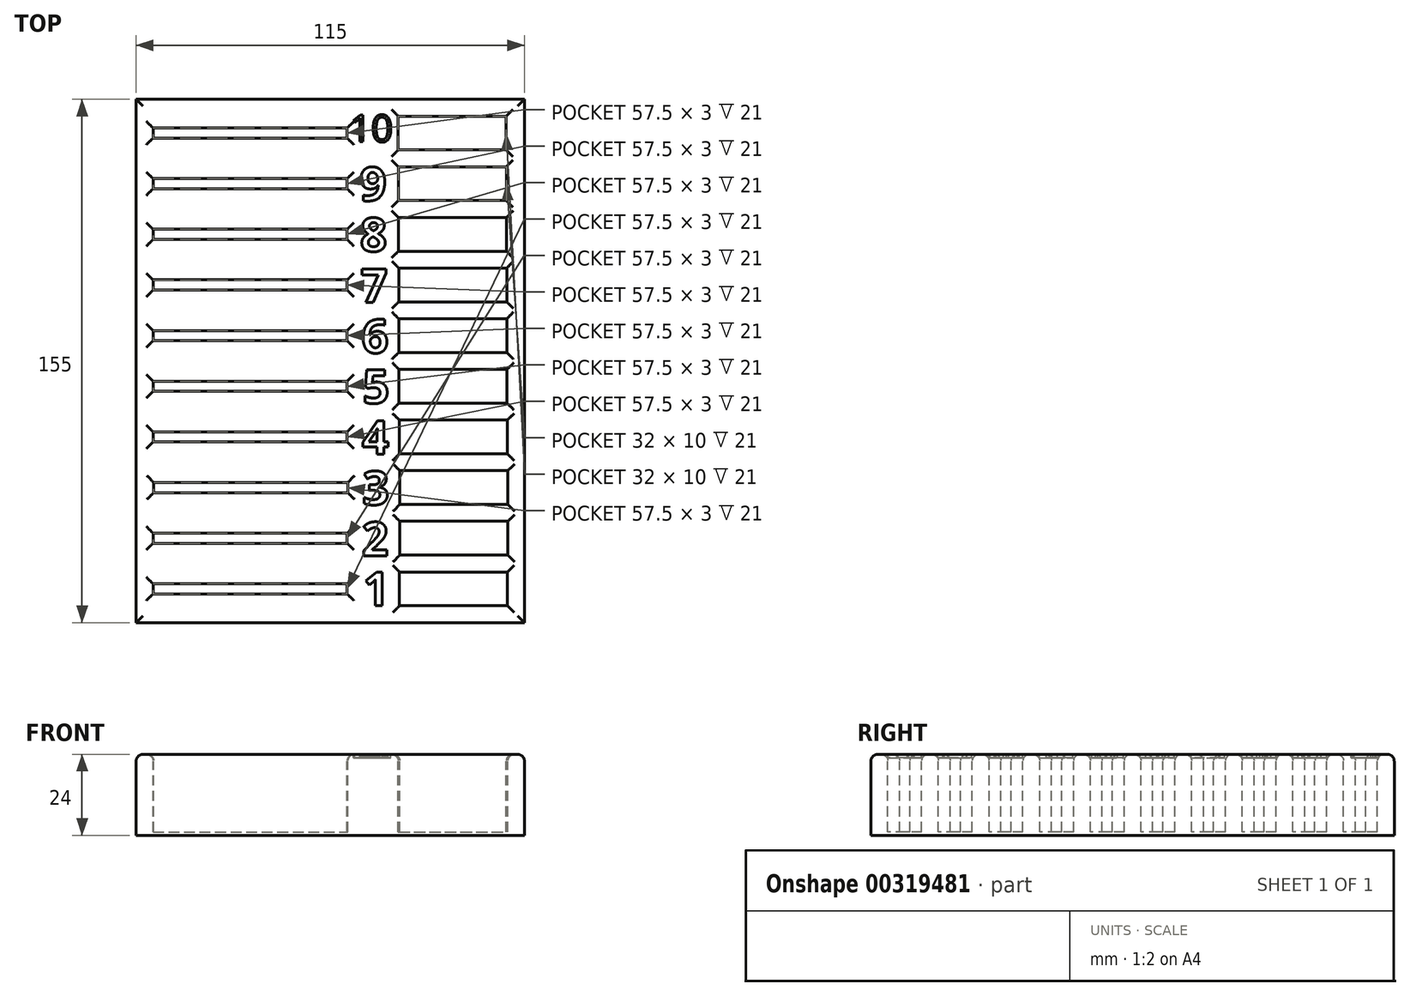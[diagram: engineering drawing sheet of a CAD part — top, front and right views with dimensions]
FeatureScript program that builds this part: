
annotation { "Feature Type Name" : "Feature", "Feature Type Description" : "" }
export const myFeature = defineFeature(function(context is Context, id is Id, definition is map)
    precondition{}
    {
        {
            var Q0;
            Q0=qCreatedBy(makeId("Top.planeOp"),FACE);
            var sketch = newSketch(context, id + "F0", { "sketchPlane" : qUnion([Q0])});
            skLineSegment(sketch, "E0.bottom", {"start": v(-49.85, 126.63) * mm, "end": v(65.15, 126.63) * mm});
            skLineSegment(sketch, "E0.top", {"start": v(-49.85, -28.37) * mm, "end": v(65.15, -28.37) * mm});
            skLineSegment(sketch, "E0.left", {"start": v(-49.85, 126.63) * mm, "end": v(-49.85, -28.37) * mm});
            skLineSegment(sketch, "E0.right", {"start": v(65.15, 126.63) * mm, "end": v(65.15, -28.37) * mm});
            skSolve(sketch);
        }
        {
            var Q0;
            Q0=makeQuery(id+"F0.imprint","IMPRINT",FACE,{"disambiguationData":[TD([[makeQuery(id+"F0.imprint","IMPRINT",EDGE,{"derivedFrom":sQuery(id+"F0.wireOp",EDGE,"E0.bottom")}),-1.0]])]});
            var Q1;
            Q1=makeQuery(id+"F0.imprint","IMPRINT",FACE,{"disambiguationData":[TD([[makeQuery(id+"F0.imprint","IMPRINT",EDGE,{"derivedFrom":sQuery(id+"F0.wireOp",EDGE,"eXpO4zti-W6eb-gkUP-Bc0d-zbJJjk6ygzeg.bottom")}),-1.0]])]});
            var Q2;
            Q2=makeQuery(id+"F0.imprint","IMPRINT",FACE,{"disambiguationData":[TD([[makeQuery(id+"F0.imprint","IMPRINT",EDGE,{"derivedFrom":sQuery(id+"F0.wireOp",EDGE,"IiJkesfC-iyIp-GpGT-9vFS-BzQ84R5pHUzr.bottom")}),-1.0]])]});
            extrude(context, id + "F1", {"entities" : qUnion([Q0, Q1, Q2]), "depth" : 24 * mm});
        }
        {
            var Q0;
            Q0=makeQuery(id+"F1.opExtrude","CAP_FACE",FACE,{"disambiguationData":[OSD([sQuery(id+"F0.wireOp",EDGE,"E0.bottom"),sQuery(id+"F0.wireOp",EDGE,"E0.top"),sQuery(id+"F0.wireOp",EDGE,"E0.left"),sQuery(id+"F0.wireOp",EDGE,"E0.right")])],"isStart":false});
            var sketch = newSketch(context, id + "F2", { "sketchPlane" : qUnion([Q0])});
            skLineSegment(sketch, "E1.bottom", {"start": v(-44.85, -16.87) * mm, "end": v(12.65, -16.87) * mm});
            skLineSegment(sketch, "E1.top", {"start": v(-44.85, -19.87) * mm, "end": v(12.65, -19.87) * mm});
            skLineSegment(sketch, "E1.left", {"start": v(-44.85, -16.87) * mm, "end": v(-44.85, -19.87) * mm});
            skLineSegment(sketch, "E1.right", {"start": v(12.65, -16.87) * mm, "end": v(12.65, -19.87) * mm});
            skLineSegment(sketch, "E2.bottom", {"start": v(28.15, -13.37) * mm, "end": v(60.15, -13.37) * mm});
            skLineSegment(sketch, "E2.top", {"start": v(28.15, -23.37) * mm, "end": v(60.15, -23.37) * mm});
            skLineSegment(sketch, "E2.left", {"start": v(28.15, -13.37) * mm, "end": v(28.15, -23.37) * mm});
            skLineSegment(sketch, "E2.right", {"start": v(60.15, -13.37) * mm, "end": v(60.15, -23.37) * mm});
            skText(sketch, "E3", { "text": "1", "fontName": "OpenSans-Bold.ttf"});
            skLineSegment(sketch, "E4.bottom", {"start": v(-44.87, -1.87) * mm, "end": v(12.63, -1.87) * mm});
            skLineSegment(sketch, "E4.top", {"start": v(-44.87, -4.87) * mm, "end": v(12.63, -4.87) * mm});
            skLineSegment(sketch, "E4.left", {"start": v(-44.87, -1.87) * mm, "end": v(-44.87, -4.87) * mm});
            skLineSegment(sketch, "E4.right", {"start": v(12.63, -1.87) * mm, "end": v(12.63, -4.87) * mm});
            skLineSegment(sketch, "E5.bottom", {"start": v(28.23, 1.63) * mm, "end": v(60.23, 1.63) * mm});
            skLineSegment(sketch, "E5.top", {"start": v(28.23, -8.37) * mm, "end": v(60.23, -8.37) * mm});
            skLineSegment(sketch, "E5.left", {"start": v(28.23, 1.63) * mm, "end": v(28.23, -8.37) * mm});
            skLineSegment(sketch, "E5.right", {"start": v(60.23, 1.63) * mm, "end": v(60.23, -8.37) * mm});
            skLineSegment(sketch, "E6.bottom", {"start": v(28.24, 16.63) * mm, "end": v(60.24, 16.63) * mm});
            skLineSegment(sketch, "E6.top", {"start": v(28.24, 6.63) * mm, "end": v(60.24, 6.63) * mm});
            skLineSegment(sketch, "E6.left", {"start": v(28.24, 16.63) * mm, "end": v(28.24, 6.63) * mm});
            skLineSegment(sketch, "E6.right", {"start": v(60.24, 16.63) * mm, "end": v(60.24, 6.63) * mm});
            skLineSegment(sketch, "E7.bottom", {"start": v(28.1, 31.63) * mm, "end": v(60.1, 31.63) * mm});
            skLineSegment(sketch, "E7.top", {"start": v(28.1, 21.63) * mm, "end": v(60.1, 21.63) * mm});
            skLineSegment(sketch, "E7.left", {"start": v(28.1, 31.63) * mm, "end": v(28.1, 21.63) * mm});
            skLineSegment(sketch, "E7.right", {"start": v(60.1, 31.63) * mm, "end": v(60.1, 21.63) * mm});
            skLineSegment(sketch, "E8.bottom", {"start": v(28, 46.63) * mm, "end": v(60, 46.63) * mm});
            skLineSegment(sketch, "E8.top", {"start": v(28, 36.63) * mm, "end": v(60, 36.63) * mm});
            skLineSegment(sketch, "E8.left", {"start": v(28, 46.63) * mm, "end": v(28, 36.63) * mm});
            skLineSegment(sketch, "E8.right", {"start": v(60, 46.63) * mm, "end": v(60, 36.63) * mm});
            skLineSegment(sketch, "E9.bottom", {"start": v(27.93, 61.63) * mm, "end": v(59.93, 61.63) * mm});
            skLineSegment(sketch, "E9.top", {"start": v(27.93, 51.63) * mm, "end": v(59.93, 51.63) * mm});
            skLineSegment(sketch, "E9.left", {"start": v(27.93, 61.63) * mm, "end": v(27.93, 51.63) * mm});
            skLineSegment(sketch, "E9.right", {"start": v(59.93, 61.63) * mm, "end": v(59.93, 51.63) * mm});
            skLineSegment(sketch, "E10.bottom", {"start": v(27.91, 76.63) * mm, "end": v(59.91, 76.63) * mm});
            skLineSegment(sketch, "E10.top", {"start": v(27.91, 66.63) * mm, "end": v(59.91, 66.63) * mm});
            skLineSegment(sketch, "E10.left", {"start": v(27.91, 76.63) * mm, "end": v(27.91, 66.63) * mm});
            skLineSegment(sketch, "E10.right", {"start": v(59.91, 76.63) * mm, "end": v(59.91, 66.63) * mm});
            skLineSegment(sketch, "E11.bottom", {"start": v(27.82, 91.63) * mm, "end": v(59.82, 91.63) * mm});
            skLineSegment(sketch, "E11.top", {"start": v(27.82, 81.63) * mm, "end": v(59.82, 81.63) * mm});
            skLineSegment(sketch, "E11.left", {"start": v(27.82, 91.63) * mm, "end": v(27.82, 81.63) * mm});
            skLineSegment(sketch, "E11.right", {"start": v(59.82, 91.63) * mm, "end": v(59.82, 81.63) * mm});
            skLineSegment(sketch, "E12.bottom", {"start": v(27.78, 106.63) * mm, "end": v(59.78, 106.63) * mm});
            skLineSegment(sketch, "E12.top", {"start": v(27.78, 96.63) * mm, "end": v(59.78, 96.63) * mm});
            skLineSegment(sketch, "E12.left", {"start": v(27.78, 106.63) * mm, "end": v(27.78, 96.63) * mm});
            skLineSegment(sketch, "E12.right", {"start": v(59.78, 106.63) * mm, "end": v(59.78, 96.63) * mm});
            skLineSegment(sketch, "E13.bottom", {"start": v(27.76, 121.63) * mm, "end": v(59.76, 121.63) * mm});
            skLineSegment(sketch, "E13.top", {"start": v(27.76, 111.63) * mm, "end": v(59.76, 111.63) * mm});
            skLineSegment(sketch, "E13.left", {"start": v(27.76, 121.63) * mm, "end": v(27.76, 111.63) * mm});
            skLineSegment(sketch, "E13.right", {"start": v(59.76, 121.63) * mm, "end": v(59.76, 111.63) * mm});
            skLineSegment(sketch, "E14.bottom", {"start": v(-44.66, 13.13) * mm, "end": v(12.84, 13.13) * mm});
            skLineSegment(sketch, "E14.top", {"start": v(-44.66, 10.13) * mm, "end": v(12.84, 10.13) * mm});
            skLineSegment(sketch, "E14.left", {"start": v(-44.66, 13.13) * mm, "end": v(-44.66, 10.13) * mm});
            skLineSegment(sketch, "E14.right", {"start": v(12.84, 13.13) * mm, "end": v(12.84, 10.13) * mm});
            skLineSegment(sketch, "E15.bottom", {"start": v(-44.85, 28.13) * mm, "end": v(12.65, 28.13) * mm});
            skLineSegment(sketch, "E15.top", {"start": v(-44.85, 25.13) * mm, "end": v(12.65, 25.13) * mm});
            skLineSegment(sketch, "E15.left", {"start": v(-44.85, 28.13) * mm, "end": v(-44.85, 25.13) * mm});
            skLineSegment(sketch, "E15.right", {"start": v(12.65, 28.13) * mm, "end": v(12.65, 25.13) * mm});
            skLineSegment(sketch, "E16.bottom", {"start": v(-44.85, 43.13) * mm, "end": v(12.65, 43.13) * mm});
            skLineSegment(sketch, "E16.top", {"start": v(-44.85, 40.13) * mm, "end": v(12.65, 40.13) * mm});
            skLineSegment(sketch, "E16.left", {"start": v(-44.85, 43.13) * mm, "end": v(-44.85, 40.13) * mm});
            skLineSegment(sketch, "E16.right", {"start": v(12.65, 43.13) * mm, "end": v(12.65, 40.13) * mm});
            skLineSegment(sketch, "E17.bottom", {"start": v(-44.85, 58.13) * mm, "end": v(12.65, 58.13) * mm});
            skLineSegment(sketch, "E17.top", {"start": v(-44.85, 55.13) * mm, "end": v(12.65, 55.13) * mm});
            skLineSegment(sketch, "E17.left", {"start": v(-44.85, 58.13) * mm, "end": v(-44.85, 55.13) * mm});
            skLineSegment(sketch, "E17.right", {"start": v(12.65, 58.13) * mm, "end": v(12.65, 55.13) * mm});
            skLineSegment(sketch, "E18.bottom", {"start": v(-44.85, 73.13) * mm, "end": v(12.65, 73.13) * mm});
            skLineSegment(sketch, "E18.top", {"start": v(-44.85, 70.13) * mm, "end": v(12.65, 70.13) * mm});
            skLineSegment(sketch, "E18.left", {"start": v(-44.85, 73.13) * mm, "end": v(-44.85, 70.13) * mm});
            skLineSegment(sketch, "E18.right", {"start": v(12.65, 73.13) * mm, "end": v(12.65, 70.13) * mm});
            skLineSegment(sketch, "E19.bottom", {"start": v(-44.85, 88.13) * mm, "end": v(12.65, 88.13) * mm});
            skLineSegment(sketch, "E19.top", {"start": v(-44.85, 85.13) * mm, "end": v(12.65, 85.13) * mm});
            skLineSegment(sketch, "E19.left", {"start": v(-44.85, 88.13) * mm, "end": v(-44.85, 85.13) * mm});
            skLineSegment(sketch, "E19.right", {"start": v(12.65, 88.13) * mm, "end": v(12.65, 85.13) * mm});
            skLineSegment(sketch, "E20.bottom", {"start": v(-44.85, 103.13) * mm, "end": v(12.65, 103.13) * mm});
            skLineSegment(sketch, "E20.top", {"start": v(-44.85, 100.13) * mm, "end": v(12.65, 100.13) * mm});
            skLineSegment(sketch, "E20.left", {"start": v(-44.85, 103.13) * mm, "end": v(-44.85, 100.13) * mm});
            skLineSegment(sketch, "E20.right", {"start": v(12.65, 103.13) * mm, "end": v(12.65, 100.13) * mm});
            skLineSegment(sketch, "E21.bottom", {"start": v(-44.85, 118.13) * mm, "end": v(12.65, 118.13) * mm});
            skLineSegment(sketch, "E21.top", {"start": v(-44.85, 115.13) * mm, "end": v(12.65, 115.13) * mm});
            skLineSegment(sketch, "E21.left", {"start": v(-44.85, 118.13) * mm, "end": v(-44.85, 115.13) * mm});
            skLineSegment(sketch, "E21.right", {"start": v(12.65, 118.13) * mm, "end": v(12.65, 115.13) * mm});
            skText(sketch, "E22", { "text": "2", "fontName": "OpenSans-Bold.ttf"});
            skText(sketch, "E23", { "text": "3", "fontName": "OpenSans-Bold.ttf"});
            skText(sketch, "E24", { "text": "4", "fontName": "OpenSans-Bold.ttf"});
            skText(sketch, "E25", { "text": "5", "fontName": "OpenSans-Bold.ttf"});
            skText(sketch, "E26", { "text": "6", "fontName": "OpenSans-Bold.ttf"});
            skText(sketch, "E27", { "text": "7", "fontName": "OpenSans-Bold.ttf"});
            skText(sketch, "E28", { "text": "8", "fontName": "OpenSans-Bold.ttf"});
            skText(sketch, "E29", { "text": "9", "fontName": "OpenSans-Bold.ttf"});
            skText(sketch, "E30", { "text": "10", "fontName": "OpenSans-Regular.ttf"});
            const initialGuessF2  = {"E3": [0.01732, -0.02332, 1, 0, 0.01], "E22": [0.01698, -0.00854, 1, 0, 0.01], "E23": [0.01713, 0.00655, 1, 0, 0.01], "E24": [0.01702, 0.02156, 1, 0, 0.01], "E25": [0.0172, 0.03658, 1, 0, 0.01], "E26": [0.01692, 0.0515, 1, 0, 0.01], "E27": [0.01664, 0.06649, 1, 0, 0.01], "E28": [0.01648, 0.08158, 1, 0, 0.01], "E29": [0.01632, 0.0966, 1, 0, 0.01], "E30": [0.01344, 0.11403, 1, 0, 0.008]};
            skSetInitialGuess(sketch, initialGuessF2);
            skSolve(sketch);
        }
        {
            var Q0;
            Q0=makeQuery(id+"F2.imprint","IMPRINT",FACE,{"disambiguationData":[TD([[makeQuery(id+"F2.imprint","IMPRINT",EDGE,{"derivedFrom":sQuery(id+"F2.wireOp",EDGE,"E2.bottom")}),-1.0]])]});
            var Q1;
            Q1=makeQuery(id+"F2.imprint","IMPRINT",FACE,{"disambiguationData":[TD([[makeQuery(id+"F2.imprint","IMPRINT",EDGE,{"derivedFrom":sQuery(id+"F2.wireOp",EDGE,"E1.bottom")}),-1.0]])]});
            var Q2;
            Q2=makeQuery(id+"F2.imprint","IMPRINT",FACE,{"disambiguationData":[TD([[makeQuery(id+"F2.imprint","IMPRINT",EDGE,{"derivedFrom":sQuery(id+"F2.wireOp",EDGE,"E4.bottom")}),-1.0]])]});
            var Q3;
            Q3=makeQuery(id+"F2.imprint","IMPRINT",FACE,{"disambiguationData":[TD([[makeQuery(id+"F2.imprint","IMPRINT",EDGE,{"derivedFrom":sQuery(id+"F2.wireOp",EDGE,"E5.bottom")}),-1.0]])]});
            var Q4;
            Q4=makeQuery(id+"F2.imprint","IMPRINT",FACE,{"disambiguationData":[TD([[makeQuery(id+"F2.imprint","IMPRINT",EDGE,{"derivedFrom":sQuery(id+"F2.wireOp",EDGE,"E6.bottom")}),-1.0]])]});
            var Q5;
            Q5=makeQuery(id+"F2.imprint","IMPRINT",FACE,{"disambiguationData":[TD([[makeQuery(id+"F2.imprint","IMPRINT",EDGE,{"derivedFrom":sQuery(id+"F2.wireOp",EDGE,"E7.bottom")}),-1.0]])]});
            var Q6;
            Q6=makeQuery(id+"F2.imprint","IMPRINT",FACE,{"disambiguationData":[TD([[makeQuery(id+"F2.imprint","IMPRINT",EDGE,{"derivedFrom":sQuery(id+"F2.wireOp",EDGE,"E8.bottom")}),-1.0]])]});
            var Q7;
            Q7=makeQuery(id+"F2.imprint","IMPRINT",FACE,{"disambiguationData":[TD([[makeQuery(id+"F2.imprint","IMPRINT",EDGE,{"derivedFrom":sQuery(id+"F2.wireOp",EDGE,"E9.bottom")}),-1.0]])]});
            var Q8;
            Q8=makeQuery(id+"F2.imprint","IMPRINT",FACE,{"disambiguationData":[TD([[makeQuery(id+"F2.imprint","IMPRINT",EDGE,{"derivedFrom":sQuery(id+"F2.wireOp",EDGE,"E10.bottom")}),-1.0]])]});
            var Q9;
            Q9=makeQuery(id+"F2.imprint","IMPRINT",FACE,{"disambiguationData":[TD([[makeQuery(id+"F2.imprint","IMPRINT",EDGE,{"derivedFrom":sQuery(id+"F2.wireOp",EDGE,"E11.bottom")}),-1.0]])]});
            var Q10;
            Q10=makeQuery(id+"F2.imprint","IMPRINT",FACE,{"disambiguationData":[TD([[makeQuery(id+"F2.imprint","IMPRINT",EDGE,{"derivedFrom":sQuery(id+"F2.wireOp",EDGE,"E12.bottom")}),-1.0]])]});
            var Q11;
            Q11=makeQuery(id+"F2.imprint","IMPRINT",FACE,{"disambiguationData":[TD([[makeQuery(id+"F2.imprint","IMPRINT",EDGE,{"derivedFrom":sQuery(id+"F2.wireOp",EDGE,"E13.bottom")}),-1.0]])]});
            var Q12;
            Q12=makeQuery(id+"F2.imprint","IMPRINT",FACE,{"disambiguationData":[TD([[makeQuery(id+"F2.imprint","IMPRINT",EDGE,{"derivedFrom":sQuery(id+"F2.wireOp",EDGE,"E14.bottom")}),-1.0]])]});
            var Q13;
            Q13=makeQuery(id+"F2.imprint","IMPRINT",FACE,{"disambiguationData":[TD([[makeQuery(id+"F2.imprint","IMPRINT",EDGE,{"derivedFrom":sQuery(id+"F2.wireOp",EDGE,"E15.bottom")}),-1.0]])]});
            var Q14;
            Q14=makeQuery(id+"F2.imprint","IMPRINT",FACE,{"disambiguationData":[TD([[makeQuery(id+"F2.imprint","IMPRINT",EDGE,{"derivedFrom":sQuery(id+"F2.wireOp",EDGE,"E16.bottom")}),-1.0]])]});
            var Q15;
            Q15=makeQuery(id+"F2.imprint","IMPRINT",FACE,{"disambiguationData":[TD([[makeQuery(id+"F2.imprint","IMPRINT",EDGE,{"derivedFrom":sQuery(id+"F2.wireOp",EDGE,"E17.bottom")}),-1.0]])]});
            var Q16;
            Q16=makeQuery(id+"F2.imprint","IMPRINT",FACE,{"disambiguationData":[TD([[makeQuery(id+"F2.imprint","IMPRINT",EDGE,{"derivedFrom":sQuery(id+"F2.wireOp",EDGE,"E18.bottom")}),-1.0]])]});
            var Q17;
            Q17=makeQuery(id+"F2.imprint","IMPRINT",FACE,{"disambiguationData":[TD([[makeQuery(id+"F2.imprint","IMPRINT",EDGE,{"derivedFrom":sQuery(id+"F2.wireOp",EDGE,"E19.bottom")}),-1.0]])]});
            var Q18;
            Q18=makeQuery(id+"F2.imprint","IMPRINT",FACE,{"disambiguationData":[TD([[makeQuery(id+"F2.imprint","IMPRINT",EDGE,{"derivedFrom":sQuery(id+"F2.wireOp",EDGE,"E20.bottom")}),-1.0]])]});
            var Q19;
            Q19=makeQuery(id+"F2.imprint","IMPRINT",FACE,{"disambiguationData":[TD([[makeQuery(id+"F2.imprint","IMPRINT",EDGE,{"derivedFrom":sQuery(id+"F2.wireOp",EDGE,"E21.bottom")}),-1.0]])]});
            extrude(context, id + "F3", {"entities" : qUnion([Q0, Q1, Q2, Q3, Q4, Q5, Q6, Q7, Q8, Q9, Q10, Q11, Q12, Q13, Q14, Q15, Q16, Q17, Q18, Q19]), "operationType" : NewBodyOperationType.REMOVE, "oppositeDirection" : true, "depth" : 23 * mm});
        }
        {
            var Q0;
            Q0=makeQuery(id+"F3.boolean.opBoolean","COPY",EDGE,{"derivedFrom":makeQuery(id+"F3.opExtrude","CAP_EDGE",EDGE,{"disambiguationData":[OSD([sQuery(id+"F2.wireOp",EDGE,"E1.top")])],"isStart":true})});
            var Q1;
            Q1=makeQuery(id+"F3.boolean.opBoolean","COPY",EDGE,{"derivedFrom":makeQuery(id+"F3.opExtrude","CAP_EDGE",EDGE,{"disambiguationData":[OSD([sQuery(id+"F2.wireOp",EDGE,"E1.bottom")])],"isStart":true})});
            var Q2;
            Q2=makeQuery(id+"F3.boolean.opBoolean","COPY",EDGE,{"derivedFrom":makeQuery(id+"F3.opExtrude","CAP_EDGE",EDGE,{"disambiguationData":[OSD([sQuery(id+"F2.wireOp",EDGE,"E1.right")])],"isStart":true})});
            var Q3;
            Q3=makeQuery(id+"F3.boolean.opBoolean","COPY",EDGE,{"derivedFrom":makeQuery(id+"F3.opExtrude","CAP_EDGE",EDGE,{"disambiguationData":[OSD([sQuery(id+"F2.wireOp",EDGE,"E1.left")])],"isStart":true})});
            var Q4;
            Q4=makeQuery(id+"F3.boolean.opBoolean","COPY",EDGE,{"derivedFrom":makeQuery(id+"F3.opExtrude","CAP_EDGE",EDGE,{"disambiguationData":[OSD([sQuery(id+"F2.wireOp",EDGE,"E2.bottom")])],"isStart":true})});
            var Q5;
            Q5=makeQuery(id+"F3.boolean.opBoolean","COPY",EDGE,{"derivedFrom":makeQuery(id+"F3.opExtrude","CAP_EDGE",EDGE,{"disambiguationData":[OSD([sQuery(id+"F2.wireOp",EDGE,"E2.top")])],"isStart":true})});
            var Q6;
            Q6=makeQuery(id+"F3.boolean.opBoolean","COPY",EDGE,{"derivedFrom":makeQuery(id+"F3.opExtrude","CAP_EDGE",EDGE,{"disambiguationData":[OSD([sQuery(id+"F2.wireOp",EDGE,"E2.left")])],"isStart":true})});
            var Q7;
            Q7=makeQuery(id+"F3.boolean.opBoolean","COPY",EDGE,{"derivedFrom":makeQuery(id+"F3.opExtrude","CAP_EDGE",EDGE,{"disambiguationData":[OSD([sQuery(id+"F2.wireOp",EDGE,"E2.right")])],"isStart":true})});
            var Q8;
            Q8=makeQuery(id+"F3.boolean.opBoolean","COPY",EDGE,{"derivedFrom":makeQuery(id+"F3.opExtrude","CAP_EDGE",EDGE,{"disambiguationData":[OSD([sQuery(id+"F2.wireOp",EDGE,"E4.bottom")])],"isStart":true})});
            var Q9;
            Q9=makeQuery(id+"F3.boolean.opBoolean","COPY",EDGE,{"derivedFrom":makeQuery(id+"F3.opExtrude","CAP_EDGE",EDGE,{"disambiguationData":[OSD([sQuery(id+"F2.wireOp",EDGE,"E4.top")])],"isStart":true})});
            var Q10;
            Q10=makeQuery(id+"F3.boolean.opBoolean","COPY",EDGE,{"derivedFrom":makeQuery(id+"F3.opExtrude","CAP_EDGE",EDGE,{"disambiguationData":[OSD([sQuery(id+"F2.wireOp",EDGE,"E4.left")])],"isStart":true})});
            var Q11;
            Q11=makeQuery(id+"F3.boolean.opBoolean","COPY",EDGE,{"derivedFrom":makeQuery(id+"F3.opExtrude","CAP_EDGE",EDGE,{"disambiguationData":[OSD([sQuery(id+"F2.wireOp",EDGE,"E4.right")])],"isStart":true})});
            var Q12;
            Q12=makeQuery(id+"F3.boolean.opBoolean","COPY",EDGE,{"derivedFrom":makeQuery(id+"F3.opExtrude","CAP_EDGE",EDGE,{"disambiguationData":[OSD([sQuery(id+"F2.wireOp",EDGE,"E5.left")])],"isStart":true})});
            var Q13;
            Q13=makeQuery(id+"F3.boolean.opBoolean","COPY",EDGE,{"derivedFrom":makeQuery(id+"F3.opExtrude","CAP_EDGE",EDGE,{"disambiguationData":[OSD([sQuery(id+"F2.wireOp",EDGE,"E5.bottom")])],"isStart":true})});
            var Q14;
            Q14=makeQuery(id+"F3.boolean.opBoolean","COPY",EDGE,{"derivedFrom":makeQuery(id+"F3.opExtrude","CAP_EDGE",EDGE,{"disambiguationData":[OSD([sQuery(id+"F2.wireOp",EDGE,"E5.right")])],"isStart":true})});
            var Q15;
            Q15=makeQuery(id+"F3.boolean.opBoolean","COPY",EDGE,{"derivedFrom":makeQuery(id+"F3.opExtrude","CAP_EDGE",EDGE,{"disambiguationData":[OSD([sQuery(id+"F2.wireOp",EDGE,"E5.top")])],"isStart":true})});
            var Q16;
            Q16=makeQuery(id+"F3.boolean.opBoolean","COPY",EDGE,{"derivedFrom":makeQuery(id+"F3.opExtrude","CAP_EDGE",EDGE,{"disambiguationData":[OSD([sQuery(id+"F2.wireOp",EDGE,"E6.top")])],"isStart":true})});
            var Q17;
            Q17=makeQuery(id+"F3.boolean.opBoolean","COPY",EDGE,{"derivedFrom":makeQuery(id+"F3.opExtrude","CAP_EDGE",EDGE,{"disambiguationData":[OSD([sQuery(id+"F2.wireOp",EDGE,"E6.left")])],"isStart":true})});
            var Q18;
            Q18=makeQuery(id+"F3.boolean.opBoolean","COPY",EDGE,{"derivedFrom":makeQuery(id+"F3.opExtrude","CAP_EDGE",EDGE,{"disambiguationData":[OSD([sQuery(id+"F2.wireOp",EDGE,"E6.bottom")])],"isStart":true})});
            var Q19;
            Q19=makeQuery(id+"F3.boolean.opBoolean","COPY",EDGE,{"derivedFrom":makeQuery(id+"F3.opExtrude","CAP_EDGE",EDGE,{"disambiguationData":[OSD([sQuery(id+"F2.wireOp",EDGE,"E6.right")])],"isStart":true})});
            var Q20;
            Q20=makeQuery(id+"F3.boolean.opBoolean","COPY",EDGE,{"derivedFrom":makeQuery(id+"F3.opExtrude","CAP_EDGE",EDGE,{"disambiguationData":[OSD([sQuery(id+"F2.wireOp",EDGE,"E7.top")])],"isStart":true})});
            var Q21;
            Q21=makeQuery(id+"F3.boolean.opBoolean","COPY",EDGE,{"derivedFrom":makeQuery(id+"F3.opExtrude","CAP_EDGE",EDGE,{"disambiguationData":[OSD([sQuery(id+"F2.wireOp",EDGE,"E7.right")])],"isStart":true})});
            var Q22;
            Q22=makeQuery(id+"F3.boolean.opBoolean","COPY",EDGE,{"derivedFrom":makeQuery(id+"F3.opExtrude","CAP_EDGE",EDGE,{"disambiguationData":[OSD([sQuery(id+"F2.wireOp",EDGE,"E7.bottom")])],"isStart":true})});
            var Q23;
            Q23=makeQuery(id+"F3.boolean.opBoolean","COPY",EDGE,{"derivedFrom":makeQuery(id+"F3.opExtrude","CAP_EDGE",EDGE,{"disambiguationData":[OSD([sQuery(id+"F2.wireOp",EDGE,"E7.left")])],"isStart":true})});
            var Q24;
            Q24=makeQuery(id+"F3.boolean.opBoolean","COPY",EDGE,{"derivedFrom":makeQuery(id+"F3.opExtrude","CAP_EDGE",EDGE,{"disambiguationData":[OSD([sQuery(id+"F2.wireOp",EDGE,"E8.left")])],"isStart":true})});
            var Q25;
            Q25=makeQuery(id+"F3.boolean.opBoolean","COPY",EDGE,{"derivedFrom":makeQuery(id+"F3.opExtrude","CAP_EDGE",EDGE,{"disambiguationData":[OSD([sQuery(id+"F2.wireOp",EDGE,"E8.bottom")])],"isStart":true})});
            var Q26;
            Q26=makeQuery(id+"F1.opExtrude","CAP_FACE",FACE,{"disambiguationData":[OSD([sQuery(id+"F0.wireOp",EDGE,"E0.bottom"),sQuery(id+"F0.wireOp",EDGE,"E0.top"),sQuery(id+"F0.wireOp",EDGE,"E0.left"),sQuery(id+"F0.wireOp",EDGE,"E0.right")])],"isStart":false});
            var Q27;
            Q27=makeQuery(id+"F3.boolean.opBoolean","COPY",EDGE,{"derivedFrom":makeQuery(id+"F3.opExtrude","CAP_EDGE",EDGE,{"disambiguationData":[OSD([sQuery(id+"F2.wireOp",EDGE,"E8.right")])],"isStart":true})});
            fillet(context, id + "F4", {"entities" : qUnion([Q0, Q1, Q2, Q3, Q4, Q5, Q6, Q7, Q8, Q9, Q10, Q11, Q12, Q13, Q14, Q15, Q16, Q17, Q18, Q19, Q20, Q21, Q22, Q23, Q24, Q25, Q26, Q27]), "radius" : 2 * mm, "tangentPropagation" : true, "allowEdgeOverflow" : false});
        }
        {
            var Q0;
            Q0=makeQuery(id+"F2.imprint","IMPRINT",FACE,{"disambiguationData":[TD([[makeQuery(id+"F2.imprint","IMPRINT",EDGE,{"derivedFrom":sQuery(id+"F2.wireOp",EDGE,"E3.sketch_text.stroke-0")}),-1.0]])]});
            var Q1;
            Q1=makeQuery(id+"F2.imprint","IMPRINT",FACE,{"disambiguationData":[TD([[makeQuery(id+"F2.imprint","IMPRINT",EDGE,{"derivedFrom":sQuery(id+"F2.wireOp",EDGE,"E22.sketch_text.stroke-0")}),-1.0]])]});
            var Q2;
            Q2=makeQuery(id+"F2.imprint","IMPRINT",FACE,{"disambiguationData":[TD([[makeQuery(id+"F2.imprint","IMPRINT",EDGE,{"derivedFrom":sQuery(id+"F2.wireOp",EDGE,"E23.sketch_text.stroke-0")}),-1.0]])]});
            var Q3;
            Q3=makeQuery(id+"F2.imprint","IMPRINT",FACE,{"disambiguationData":[TD([[makeQuery(id+"F2.imprint","IMPRINT",EDGE,{"derivedFrom":sQuery(id+"F2.wireOp",EDGE,"E24.sketch_text.stroke-0")}),-1.0]])]});
            var Q4;
            Q4=makeQuery(id+"F2.imprint","IMPRINT",FACE,{"disambiguationData":[TD([[makeQuery(id+"F2.imprint","IMPRINT",EDGE,{"derivedFrom":sQuery(id+"F2.wireOp",EDGE,"E25.sketch_text.stroke-0")}),-1.0]])]});
            var Q5;
            Q5=makeQuery(id+"F2.imprint","IMPRINT",FACE,{"disambiguationData":[TD([[makeQuery(id+"F2.imprint","IMPRINT",EDGE,{"derivedFrom":sQuery(id+"F2.wireOp",EDGE,"E26.sketch_text.stroke-0")}),-1.0]])]});
            var Q6;
            Q6=makeQuery(id+"F2.imprint","IMPRINT",FACE,{"disambiguationData":[TD([[makeQuery(id+"F2.imprint","IMPRINT",EDGE,{"derivedFrom":sQuery(id+"F2.wireOp",EDGE,"E27.sketch_text.stroke-0")}),-1.0]])]});
            var Q7;
            Q7=makeQuery(id+"F2.imprint","IMPRINT",FACE,{"disambiguationData":[TD([[makeQuery(id+"F2.imprint","IMPRINT",EDGE,{"derivedFrom":sQuery(id+"F2.wireOp",EDGE,"E28.sketch_text.stroke-0")}),-1.0]])]});
            var Q8;
            Q8=makeQuery(id+"F2.imprint","IMPRINT",FACE,{"disambiguationData":[TD([[makeQuery(id+"F2.imprint","IMPRINT",EDGE,{"derivedFrom":sQuery(id+"F2.wireOp",EDGE,"E29.sketch_text.stroke-0")}),-1.0]])]});
            var Q9;
            Q9=makeQuery(id+"F2.imprint","IMPRINT",FACE,{"disambiguationData":[TD([[makeQuery(id+"F2.imprint","IMPRINT",EDGE,{"derivedFrom":sQuery(id+"F2.wireOp",EDGE,"E30.sketch_text.stroke-0")}),-1.0]])]});
            var Q10;
            Q10=makeQuery(id+"F2.imprint","IMPRINT",FACE,{"disambiguationData":[TD([[makeQuery(id+"F2.imprint","IMPRINT",EDGE,{"derivedFrom":sQuery(id+"F2.wireOp",EDGE,"E30.sketch_text.stroke-9")}),-1.0]])]});
            extrude(context, id + "F5", {"entities" : qUnion([Q0, Q1, Q2, Q3, Q4, Q5, Q6, Q7, Q8, Q9, Q10]), "operationType" : NewBodyOperationType.REMOVE, "oppositeDirection" : true, "depth" : 1 * mm});
        }
    });
